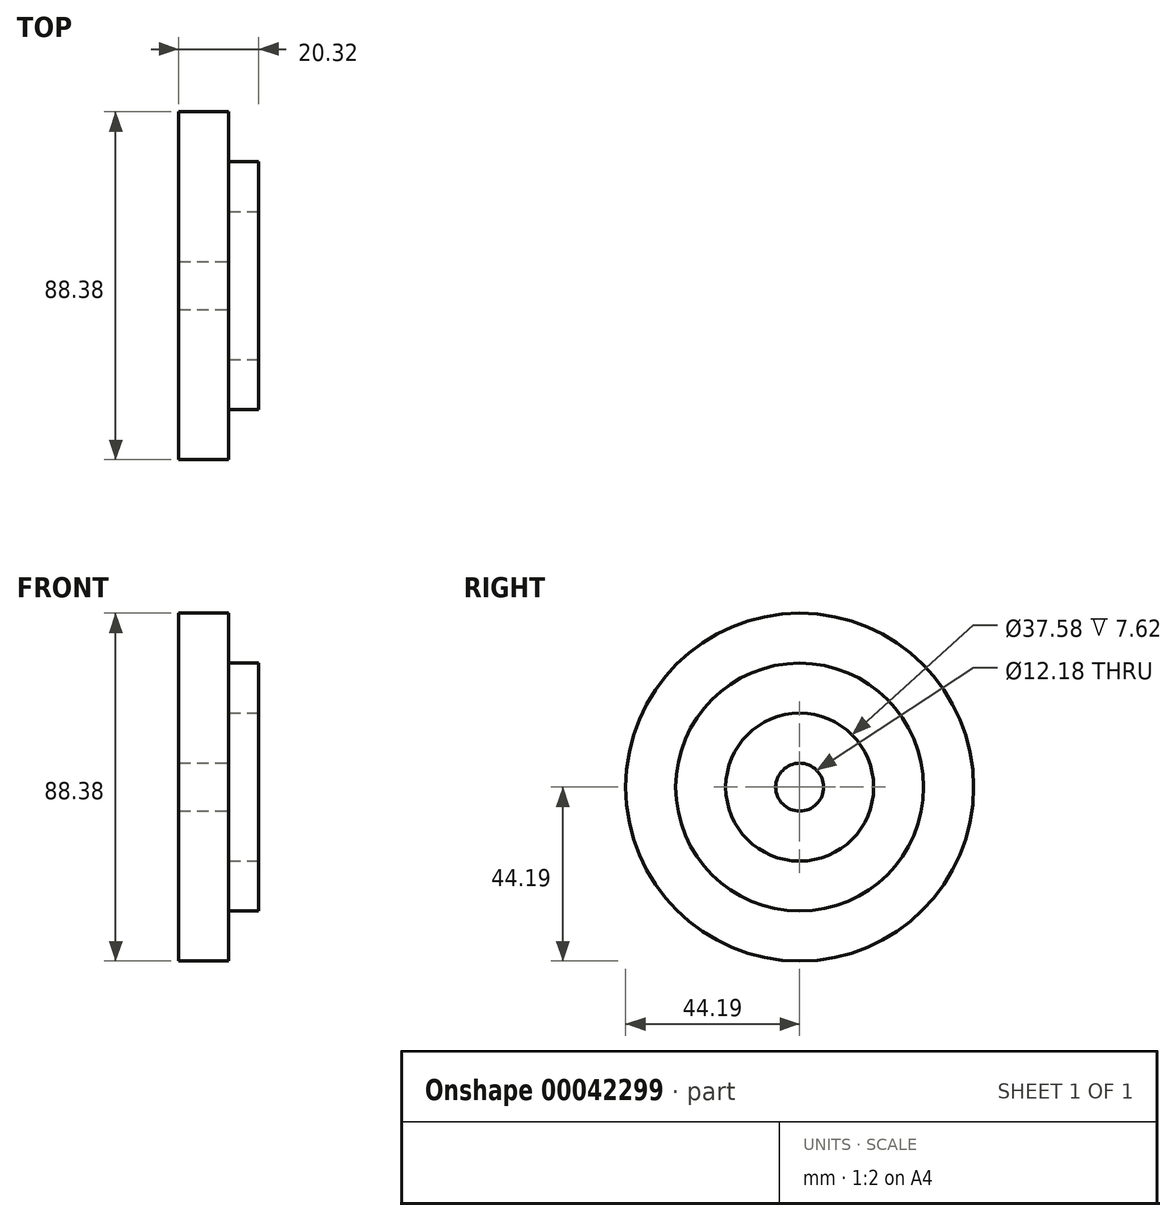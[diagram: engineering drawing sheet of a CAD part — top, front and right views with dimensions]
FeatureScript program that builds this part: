
annotation { "Feature Type Name" : "Feature", "Feature Type Description" : "" }
export const myFeature = defineFeature(function(context is Context, id is Id, definition is map)
    precondition{}
    {
        {
            var Q0;
            Q0=qCreatedBy(makeId("Front.planeOp"),FACE);
            var sketch = newSketch(context, id + "F0", { "sketchPlane" : qUnion([Q0])});
            skLineSegment(sketch, "E0", {"start": v(0, 44.19) * mm, "end": v(0, 6.09) * mm});
            skLineSegment(sketch, "E1", {"start": v(0, 6.09) * mm, "end": v(12.7, 6.09) * mm});
            skLineSegment(sketch, "E2", {"start": v(12.7, 6.09) * mm, "end": v(12.7, 18.79) * mm});
            skLineSegment(sketch, "E3", {"start": v(12.7, 18.79) * mm, "end": v(20.32, 18.79) * mm});
            skLineSegment(sketch, "E4", {"start": v(20.32, 18.79) * mm, "end": v(20.32, 31.49) * mm});
            skLineSegment(sketch, "E5", {"start": v(20.32, 31.49) * mm, "end": v(12.7, 31.49) * mm});
            skLineSegment(sketch, "E6", {"start": v(12.7, 31.49) * mm, "end": v(12.7, 44.19) * mm});
            skLineSegment(sketch, "E7", {"start": v(12.7, 44.19) * mm, "end": v(0, 44.19) * mm});
            skLineSegment(sketch, "E8", {"start": v(-41.02, 0) * mm, "end": v(44.93, 0) * mm});
            skSolve(sketch);
        }
        {
            var Q0;
            Q0=sQuery(id+"F0.wireOp",EDGE,"E0");
            var Q1;
            Q1=sQuery(id+"F0.wireOp",EDGE,"E7");
            var Q2;
            Q2=sQuery(id+"F0.wireOp",EDGE,"E6");
            var Q3;
            Q3=sQuery(id+"F0.wireOp",EDGE,"E5");
            var Q4;
            Q4=sQuery(id+"F0.wireOp",EDGE,"E3");
            var Q5;
            Q5=sQuery(id+"F0.wireOp",EDGE,"E4");
            var Q6;
            Q6=sQuery(id+"F0.wireOp",EDGE,"E1");
            var Q7;
            Q7=sQuery(id+"F0.wireOp",EDGE,"E2");
            var Q8;
            Q8=sQuery(id+"F0.wireOp",EDGE,"E8");
            revolve(context, id + "F1", {"bodyType" : ToolBodyType.SURFACE, "surfaceEntities" : qUnion([Q0, Q1, Q2, Q3, Q4, Q5, Q6, Q7]), "axis" : qUnion([Q8]), "revolveType" : RevolveType.FULL});
        }
    });
